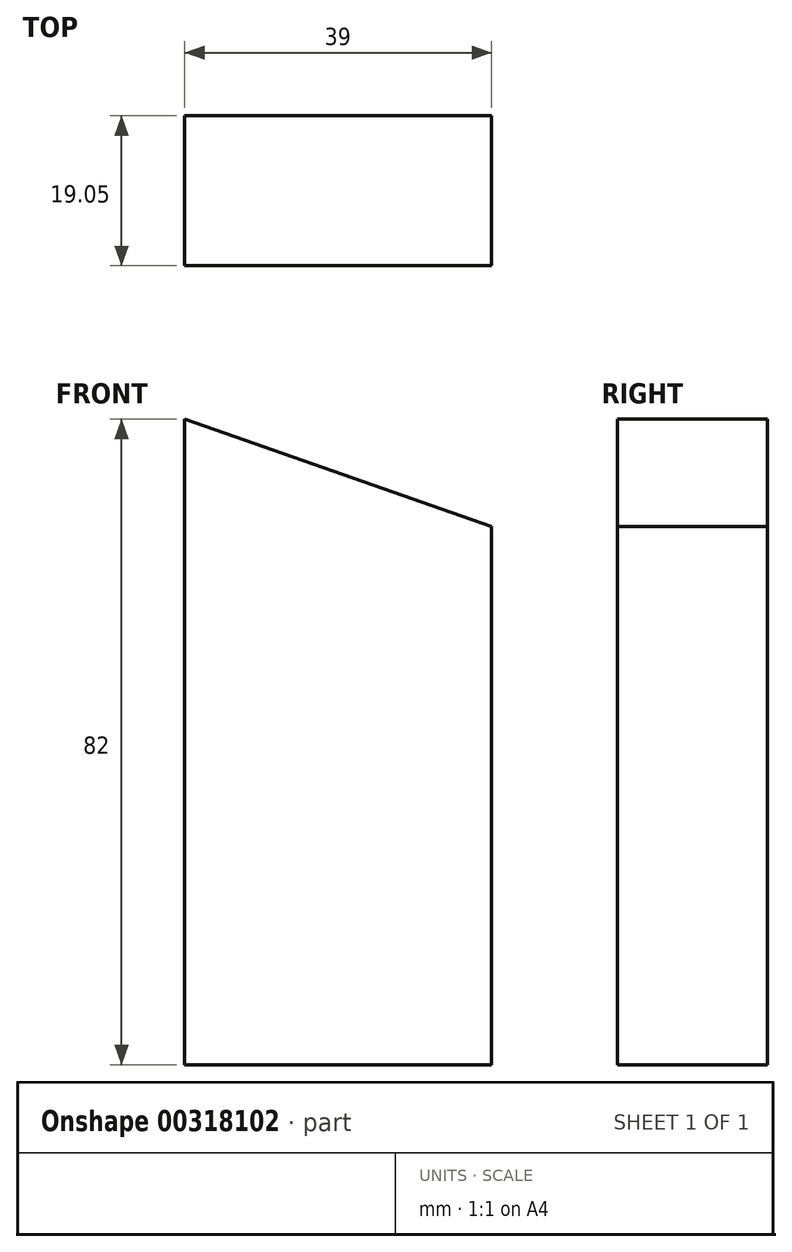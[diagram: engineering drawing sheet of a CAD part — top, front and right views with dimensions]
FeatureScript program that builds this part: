
annotation { "Feature Type Name" : "Feature", "Feature Type Description" : "" }
export const myFeature = defineFeature(function(context is Context, id is Id, definition is map)
    precondition{}
    {
        {
            var Q0;
            Q0=qCreatedBy(makeId("Front.planeOp"),FACE);
            var sketch = newSketch(context, id + "F0", { "sketchPlane" : qUnion([Q0])});
            skLineSegment(sketch, "E0", {"start": v(0, 0) * mm, "end": v(25.4, 0) * mm, "construction": true});
            skLineSegment(sketch, "E1", {"start": v(0, 0) * mm, "end": v(-25.4, 0) * mm, "construction": true});
            skCircle(sketch, "E2", {"center": v(-25.4, 0) * mm, "radius": 11 * mm});
            skCircle(sketch, "E3", {"center": v(25.4, 0) * mm, "radius": 11 * mm});
            skLineSegment(sketch, "E4", {"start": v(25.4, 21) * mm, "end": v(-85.4, 21) * mm});
            skLineSegment(sketch, "E5", {"start": v(25.4, -21) * mm, "end": v(-85.4, -21) * mm});
            skLineSegment(sketch, "E6", {"start": v(-85.4, 21) * mm, "end": v(-85.4, -21) * mm});
            skLineSegment(sketch, "E7", {"start": v(-85.4, 61) * mm, "end": v(-85.4, 21) * mm});
            skArc(sketch, "E8", {"start": v(25.4, -21) * mm, "mid": v(46.4, 0) * mm, "end": v(25.4, 21) * mm});
            skLineSegment(sketch, "E9", {"start": v(-85.4, 61) * mm, "end": v(32.33, 19.82) * mm});
            skSolve(sketch);
        }
        {
            var Q0;
            Q0=qSketchRegion(id+"F0",true);
            extrude(context, id + "F1", {"entities" : qUnion([Q0]), "endBound" : BoundingType.SYMMETRIC, "depth" : 7 * mm});
        }
        {
            var Q0;
            Q0=makeQuery(id+"F1.opExtrude","CAP_FACE",FACE,{"disambiguationData":[OSD([sQuery(id+"F0.wireOp",EDGE,"E2"),sQuery(id+"F0.wireOp",EDGE,"E3"),sQuery(id+"F0.wireOp",EDGE,"E5"),sQuery(id+"F0.wireOp",EDGE,"E6"),sQuery(id+"F0.wireOp",EDGE,"E7"),sQuery(id+"F0.wireOp",EDGE,"E8"),sQuery(id+"F0.wireOp",EDGE,"E9")])],"isStart":false});
            var sketch = newSketch(context, id + "F2", { "sketchPlane" : qUnion([Q0])});
            skCircle(sketch, "E10.0", {"center": v(-25.4, 0) * mm, "radius": 11 * mm});
            skLineSegment(sketch, "E10.1", {"start": v(-85.4, 61) * mm, "end": v(32.33, 19.82) * mm});
            skArc(sketch, "E10.2", {"start": v(25.4, -21) * mm, "mid": v(46.1, -3.52) * mm, "end": v(32.33, 19.82) * mm});
            skLineSegment(sketch, "E11.0", {"start": v(-85.4, 61) * mm, "end": v(-85.4, -21) * mm});
            skLineSegment(sketch, "E12.0", {"start": v(25.4, -21) * mm, "end": v(-85.4, -21) * mm});
            skLineSegment(sketch, "E13", {"start": v(-46.4, -21) * mm, "end": v(-46.4, 47.36) * mm});
            skSolve(sketch);
        }
        {
            var Q0;
            {var subQ0=sQuery(id+"F2.wireOp",EDGE,"E11.0");Q0=makeQuery(id+"F2.imprint","IMPRINT",FACE,{"disambiguationData":[TD([[makeQuery(id+"F2.imprint","IMPRINT",EDGE,{"derivedFrom":subQ0}),1.0]])]});}
            extrude(context, id + "F3", {"entities" : qUnion([Q0]), "depth" : 19.05 * mm, "offsetDistance" : 25.4 * mm});
        }
        {
            var Q0;
            Q0=makeQuery(id+"F3.opExtrude","SWEPT_BODY",BODY,{"disambiguationData":[OSD([sQuery(id+"F2.wireOp",EDGE,"E10.1"),sQuery(id+"F2.wireOp",EDGE,"E11.0"),sQuery(id+"F2.wireOp",EDGE,"E12.0"),sQuery(id+"F2.wireOp",EDGE,"E13")])]});
            var Q1;
            Q1=qCreatedBy(makeId("Front.planeOp"),FACE);
            mirror(context, id + "F4", {"entities" : qUnion([Q0]), "mirrorPlane" : qUnion([Q1])});
        }
        {
            var Q0;
            Q0=makeQuery(id+"F1.opExtrude","SWEPT_BODY",BODY,{"disambiguationData":[OSD([sQuery(id+"F0.wireOp",EDGE,"E2"),sQuery(id+"F0.wireOp",EDGE,"E3"),sQuery(id+"F0.wireOp",EDGE,"E5"),sQuery(id+"F0.wireOp",EDGE,"E6"),sQuery(id+"F0.wireOp",EDGE,"E7"),sQuery(id+"F0.wireOp",EDGE,"E8"),sQuery(id+"F0.wireOp",EDGE,"E9")])]});
            var Q1;
            Q1=makeQuery(id+"F3.opExtrude","SWEPT_BODY",BODY,{"disambiguationData":[OSD([sQuery(id+"F2.wireOp",EDGE,"E10.1"),sQuery(id+"F2.wireOp",EDGE,"E11.0"),sQuery(id+"F2.wireOp",EDGE,"E12.0"),sQuery(id+"F2.wireOp",EDGE,"E13")])]});
            deleteBodies(context, id + "F5", {"entities" : qUnion([Q0, Q1])});
        }
    });
